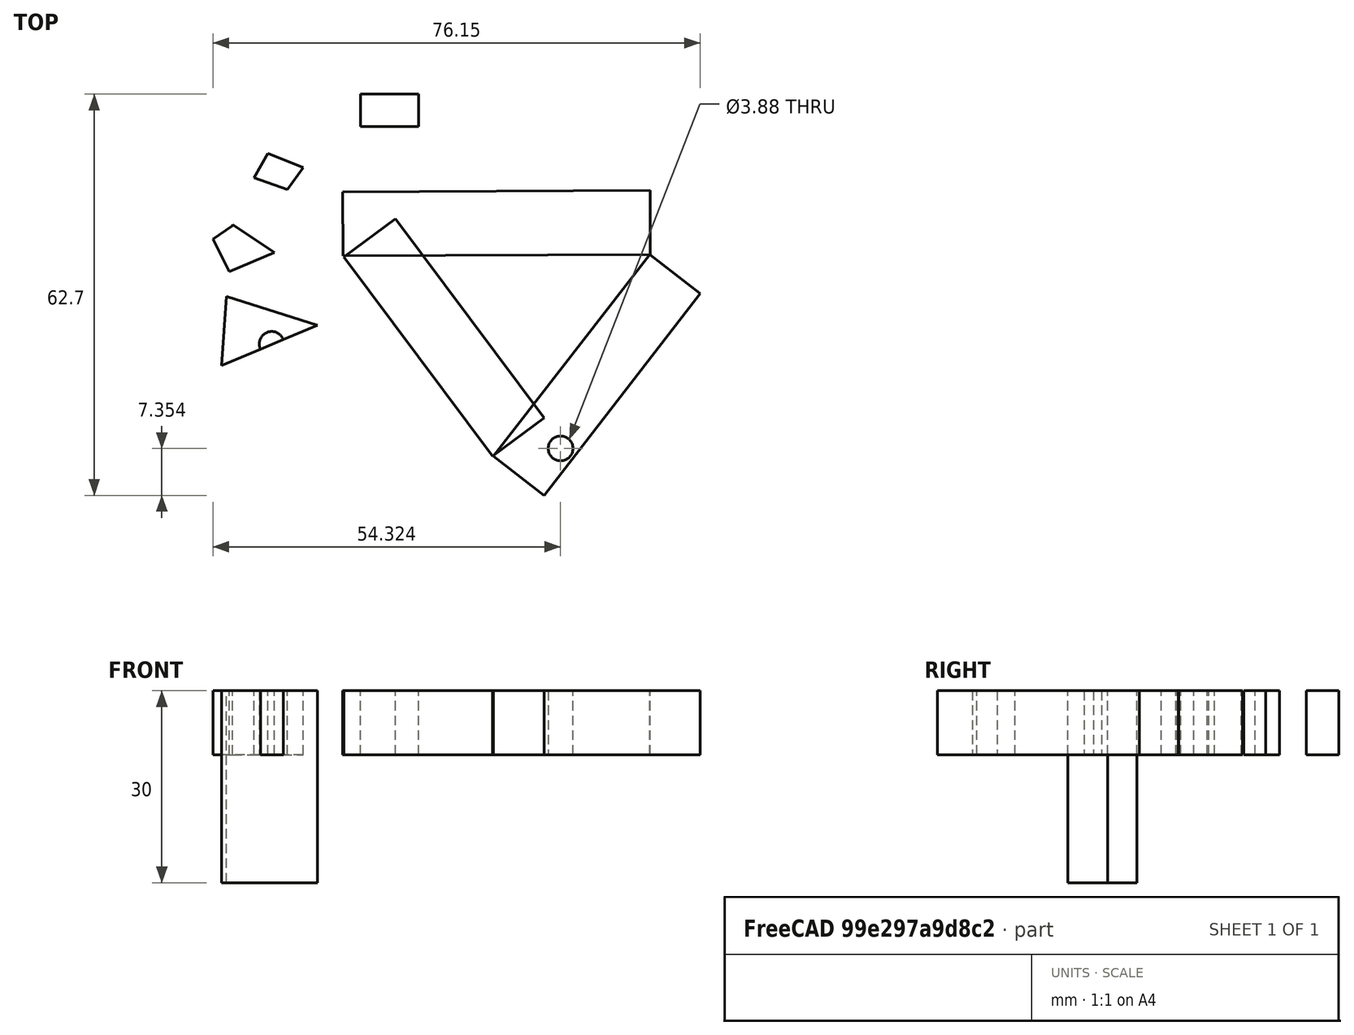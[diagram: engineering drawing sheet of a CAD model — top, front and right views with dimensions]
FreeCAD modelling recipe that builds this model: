
FCSTD DOCUMENT  (FreeCAD 1.0R39285 (Git))
Label: test01
License: All rights reserved
objects: Part::Extrusion×12, Part::Part2DObjectPython×10, Part::FeaturePython×2, Part::Cut×2, App::Part×1, Sketcher::SketchObject×1, App::DocumentObjectGroup×1
note: 28 computed .brp shape members not serialized (recipe doc carries the construction recipe); baked Part::Feature solids carry a one-line shape summary decoded from their .brp

FEATURE [App::Part] Part001
  Origin = -> Origin001
FEATURE [Part::Part2DObjectPython] Line  # Draft 2D object (typed FeaturePython)
  Area = 0
  ChamferSize = 0
  Closed = false
  End = (24.5325,18.5681,0)
  FilletRadius = 0
  Length = 48.0608
  MakeFace = true
  Placement = pos=(-23.5276,18.3305,0) rot=(0,0,1;0rad)
  Points = (2) [(0,0,0),(48.0602,0.237532,0)]
  Start = (-23.5276,18.3305,0)
  Subdivisions = 0
FEATURE [Part::Part2DObjectPython] Line001  # Draft 2D object (typed FeaturePython)
  Area = 0
  ChamferSize = 0
  Closed = false
  End = (0.00718539,-12.9873,0)
  FilletRadius = 0
  Length = 39.8737
  MakeFace = true
  Placement = pos=(24.4211,18.5385,0) rot=(0,0,1;0rad)
  Points = (2) [(0,0,0),(-24.4139,-31.5257,0)]
  Start = (24.4211,18.5385,0)
  Subdivisions = 0
FEATURE [Part::Part2DObjectPython] Line002  # Draft 2D object (typed FeaturePython)
  Area = 0
  ChamferSize = 0
  Closed = false
  End = (-0.0989609,-12.9873,0)
  FilletRadius = 0
  Length = 38.8713
  MakeFace = true
  Placement = pos=(-23.3452,18.167,0) rot=(0,0,1;0rad)
  Points = (2) [(0,0,0),(23.2463,-31.1542,0)]
  Start = (-23.3452,18.167,0)
  Subdivisions = 0
FEATURE [Part::Extrusion] Extrude
  Base = -> Line
  Dir = (0,0,1)
  DirMode = 2
  FaceMakerClass = Part::FaceMakerBullseye
  FaceMakerMode = 3
  LengthFwd = 10
  LengthRev = 0
  Solid = false
  Symmetric = false
FEATURE [Part::Extrusion] Extrude001
  Base = -> Line001
  Dir = (0,0,1)
  DirMode = 2
  FaceMakerClass = Part::FaceMakerBullseye
  FaceMakerMode = 3
  LengthFwd = 10
  LengthRev = 0
  Solid = false
  Symmetric = false
FEATURE [Part::Extrusion] Extrude002
  Base = -> Line002
  Dir = (0,0,1)
  DirMode = 2
  FaceMakerClass = Part::FaceMakerBullseye
  FaceMakerMode = 3
  LengthFwd = 10
  LengthRev = 0
  Solid = false
  Symmetric = false
FEATURE [Part::FeaturePython] Facebinder  # WARN: FeaturePython — macro-defined, semantics opaque (R4)
  Area = 0
  Extrusion = 0
  RemoveSplitter = false
  Sew = false
FEATURE [Part::FeaturePython] Hatch  # WARN: FeaturePython — macro-defined, semantics opaque (R4)
  Base = -> Extrude002
  Rotation = 0
  Scale = 100
  Translate = true
FEATURE [Part::Extrusion] Extrude003
  Base = -> Extrude
  Dir = (-0.00494232,0.999988,0)
  DirMode = 2
  FaceMakerClass = Part::FaceMakerBullseye
  FaceMakerMode = 3
  LengthFwd = 10
  LengthRev = 0
  Solid = false
  Symmetric = false
FEATURE [Part::Extrusion] Extrude004
  Base = -> Extrude001
  Dir = (0.790641,-0.612281,0)
  DirMode = 2
  FaceMakerClass = Part::FaceMakerBullseye
  FaceMakerMode = 3
  LengthFwd = 10
  LengthRev = 0
  Solid = false
  Symmetric = false
FEATURE [Part::Extrusion] Extrude005
  Base = -> Extrude002
  Dir = (0.801472,0.598032,0)
  DirMode = 2
  FaceMakerClass = Part::FaceMakerBullseye
  FaceMakerMode = 3
  LengthFwd = 10
  LengthRev = 0
  Solid = false
  Symmetric = false
FEATURE [Sketcher::SketchObject] Sketch
  ArcFitTolerance = 1e-06
  AttachmentSupport = -> [Extrude002,Extrude001,Extrude]
  FullyConstrained = true
  MakeInternals = false
  MapMode = 45
  Placement = pos=(0.43782,8.65917,10) rot=(0,0,1;1.6086rad)
FEATURE [Part::Part2DObjectPython] Rectangle  # Draft 2D object (typed FeaturePython)
  Area = 45.7622
  ChamferSize = 0
  Columns = 1
  FilletRadius = 0
  Height = 5.05402
  Length = 9.05461
  MakeFace = true
  Placement = pos=(-20.7495,38.5391,0) rot=(0,0,1;0rad)
  Rows = 1
FEATURE [Part::Extrusion] Extrude006
  Base = -> Rectangle
  Dir = (0,0,1)
  DirMode = 2
  FaceMakerClass = Part::FaceMakerBullseye
  FaceMakerMode = 3
  LengthFwd = 10
  LengthRev = 0
  Solid = false
  Symmetric = false
FEATURE [Part::Part2DObjectPython] Line006  # Draft 2D object (typed FeaturePython)
  Area = 0
  ChamferSize = 0
  Closed = false
  End = (-15.2612,51.1821,0)
  FilletRadius = 0
  Length = 6.87368
  MakeFace = true
  Points = (2) [(-21.3999,54.2747,0),(-15.2612,51.1821,0)]
  Start = (-21.3999,54.2747,0)
  Subdivisions = 0
FEATURE [Part::Part2DObjectPython] Wire  # Draft 2D object (typed FeaturePython)
  Area = 23.9676
  ChamferSize = 0
  Closed = true
  End = (-37.4027,30.5237,0)
  FilletRadius = 0
  Length = 20.034
  MakeFace = true
  Placement = pos=(-35.2752,34.3175,0) rot=(0,0,1;0rad)
  Points = (4) [(0,0,0),(5.5461,-2.17053,0),(3.0642,-5.59853,0),(-2.12755,-3.79382,0)]
  Start = (-35.2752,34.3175,0)
  Subdivisions = 0
FEATURE [Part::Extrusion] Extrude007
  Base = -> Wire
  Dir = (0,0,1)
  DirMode = 2
  FaceMakerClass = Part::FaceMakerBullseye
  FaceMakerMode = 3
  LengthFwd = 10
  LengthRev = 0
  Solid = false
  Symmetric = false
FEATURE [Part::Part2DObjectPython] Wire001  # Draft 2D object (typed FeaturePython)
  Area = 35.4965
  ChamferSize = 0
  Closed = true
  End = (-40.7587,23.0223,0)
  FilletRadius = 0
  Length = 25.1437
  MakeFace = true
  Placement = pos=(-40.7955,23.2568,-1.8e-15) rot=(0,0,1;0rad)
  Points = (5) [(0,0,0),(6.5353,-4.38496,1.77636e-15),(-0.492353,-7.40381,0),(-3.02171,-2.29742,1.77636e-15),(0.0367884,-0.234502,1.77636e-15)]
  Start = (-40.7955,23.2568,-1.8e-15)
  Subdivisions = 0
FEATURE [Part::Part2DObjectPython] Wire002  # Draft 2D object (typed FeaturePython)
  Area = 78.5429
  ChamferSize = 0
  Closed = true
  End = (-42.5043,1.22544,0)
  FilletRadius = 0
  Length = 42.0194
  MakeFace = true
  Placement = pos=(-41.7285,12.0126,-1.8e-15) rot=(0,0,1;0rad)
  Points = (3) [(0,0,0),(14.2366,-4.52804,1.77636e-15),(-0.775791,-10.7872,1.77636e-15)]
  Start = (-41.7285,12.0126,-1.8e-15)
  Subdivisions = 0
FEATURE [Part::Extrusion] Extrude008
  Base = -> Wire002
  Dir = (0,0,1)
  DirMode = 2
  FaceMakerClass = Part::FaceMakerBullseye
  FaceMakerMode = 3
  LengthFwd = 10
  LengthRev = 20
  Solid = false
  Symmetric = false
FEATURE [Part::Extrusion] Extrude009
  Base = -> Wire001
  Dir = (0,0,1)
  DirMode = 2
  FaceMakerClass = Part::FaceMakerBullseye
  FaceMakerMode = 3
  LengthFwd = 10
  LengthRev = 0
  Solid = false
  Symmetric = false
FEATURE [Part::Part2DObjectPython] Circle  # Draft 2D object (typed FeaturePython)
  Area = 11.8737
  FirstAngle = 0
  LastAngle = 0
  MakeFace = true
  Placement = pos=(-34.6487,4.56885,0) rot=(0,0,1;0rad)
  Radius = 1.9441
FEATURE [Part::Extrusion] Extrude010
  Base = -> Circle
  Dir = (0,0,1)
  DirMode = 2
  FaceMakerClass = Part::FaceMakerBullseye
  FaceMakerMode = 3
  LengthFwd = 100
  LengthRev = 0
  Solid = false
  Symmetric = false
FEATURE [Part::Cut] Cut
  Base = -> Extrude008
  Tool = -> Extrude010
FEATURE [Part::Part2DObjectPython] Circle001  # Draft 2D object (typed FeaturePython)
  Area = 11.7936
  FirstAngle = 0
  LastAngle = 0
  MakeFace = true
  Placement = pos=(10.504,-11.756,0) rot=(0,0,1;0rad)
  Radius = 1.93753
FEATURE [App::DocumentObjectGroup] Draft_Construction  label="Construction"
  Group = -> [Line,Line001,Line002,Rectangle,Line006,Wire,Wire001,Wire002,Circle,Circle001]
FEATURE [Part::Extrusion] Extrude011
  Base = -> Circle001
  Dir = (0,0,1)
  DirMode = 2
  FaceMakerClass = Part::FaceMakerBullseye
  FaceMakerMode = 3
  LengthFwd = 10
  LengthRev = 0
  Solid = false
  Symmetric = false
FEATURE [Part::Cut] Cut001
  Base = -> Extrude004
  Tool = -> Extrude011
